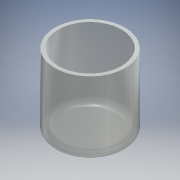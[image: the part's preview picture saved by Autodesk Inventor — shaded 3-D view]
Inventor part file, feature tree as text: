
AUTODESK INVENTOR PART (.ipt)
format: ipt  version: 2016 (Build 200138000, 138)  size: 159,232 bytes
history: native  units: mm
features: other x2, revolve x1, sketch x1
ambient origin geometry x8: Origin, YZ Plane, XZ Plane, XY Plane, X Axis, Y Axis, Z Axis, Center Point
bodies: Body1 (feature_tree)
feature tree (4):
  other  "Sólido1"
  revolve  "Revolución1"  [1 undecoded]
  other  "Desplazar cuerpo1"
  sketch  "Boceto2"  dims[d4=5.0mm d5=100.0mm d6=5.0mm d7=48.0mm d8=90.0deg d9=10.0mm d10=8.0mm d11=90.0deg]
note: 1 required parameter value undecoded (feature->parameter linkage not recoverable at this tier; creation-order binding heuristic only, values carry confidence <= 0.55)
